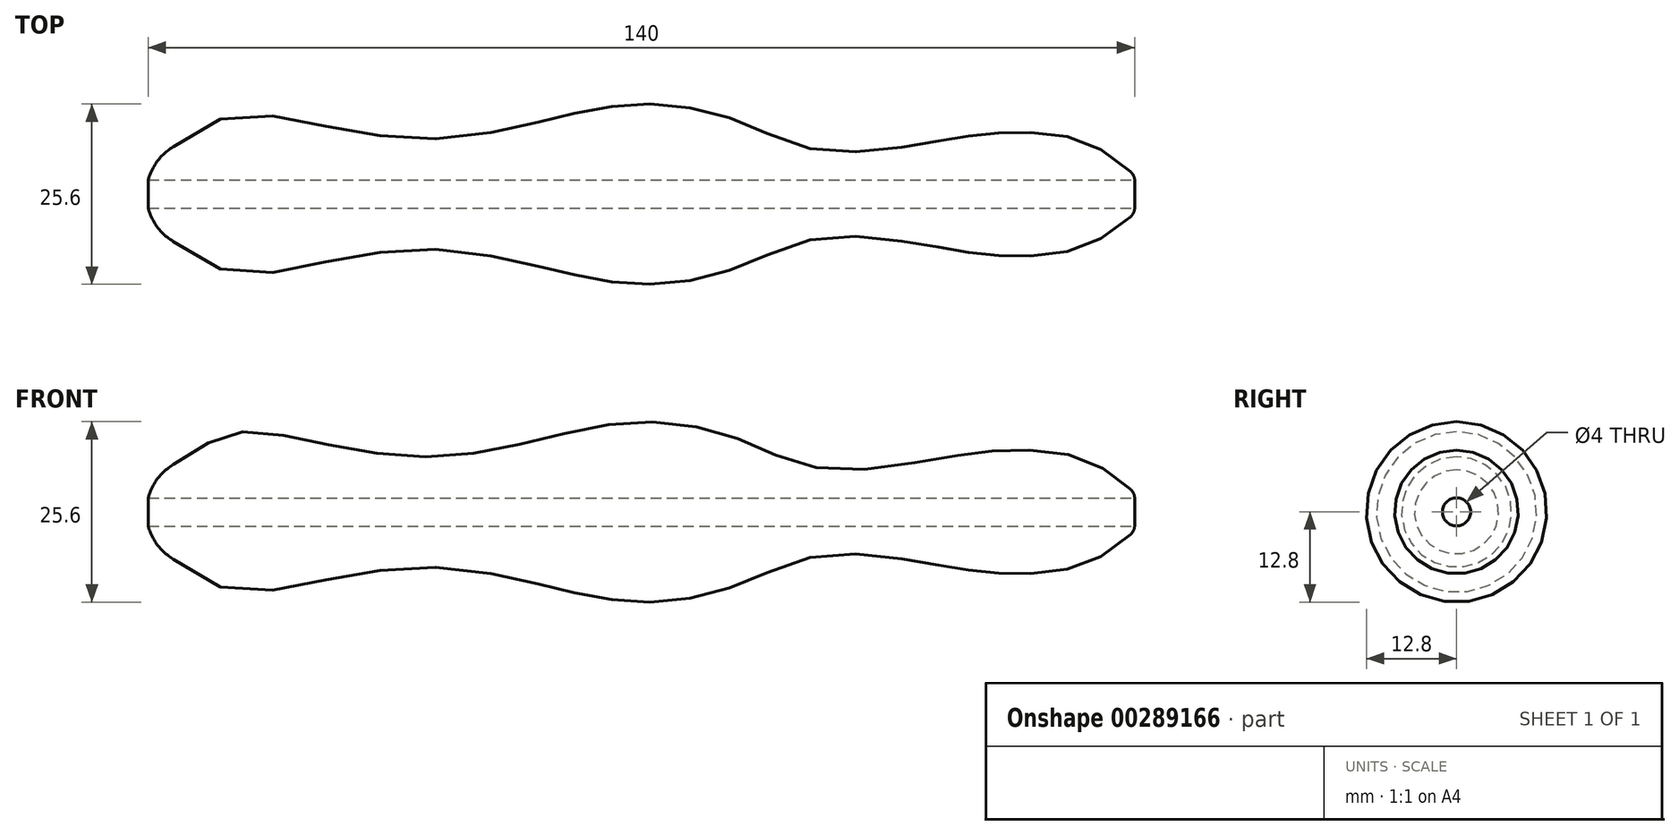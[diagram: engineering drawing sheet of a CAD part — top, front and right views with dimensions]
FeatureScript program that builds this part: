
annotation { "Feature Type Name" : "Feature", "Feature Type Description" : "" }
export const myFeature = defineFeature(function(context is Context, id is Id, definition is map)
    precondition{}
    {
        {
            var Q0;
            Q0=qCreatedBy(makeId("Top.planeOp"),FACE);
            var sketch = newSketch(context, id + "F0", { "sketchPlane" : qUnion([Q0])});
            skLineSegment(sketch, "E0", {"start": v(0, 0) * mm, "end": v(140, 0) * mm});
            skLineSegment(sketch, "E1", {"start": v(140, 2.71) * mm, "end": v(140, 0) * mm});
            skLineSegment(sketch, "E2", {"start": v(0, 0) * mm, "end": v(0, 5) * mm});
            skFitSpline(sketch, "E3", {"points": [v(0, 5) * mm, v(11.1, 10.96) * mm, v(23.25, 10.04) * mm, v(40.19, 7.83) * mm, v(56.02, 10.4) * mm, v(70.2, 12.8) * mm, v(83.64, 10.4) * mm, v(95.61, 6.17) * mm, v(112.74, 7.64) * mm, v(121.95, 8.75) * mm, v(132.81, 7.46) * mm, v(140, 2.71) * mm], "startDerivative": vector(166.86, 63.4) * mm, "endDerivative": vector(86.8, -71.08) * mm});
            skSolve(sketch);
        }
        {
            var Q0;
            Q0=makeQuery(id+"F0.imprint","IMPRINT",FACE,{"disambiguationData":[TD([[makeQuery(id+"F0.imprint","IMPRINT",EDGE,{"derivedFrom":sQuery(id+"F0.wireOp",EDGE,"E0")}),1.0]])]});
            var Q1;
            Q1=sQuery(id+"F0.wireOp",EDGE,"E0");
            revolve(context, id + "F1", {"entities" : qUnion([Q0]), "axis" : qUnion([Q1]), "revolveType" : RevolveType.FULL});
        }
        {
            var Q0;
            Q0=makeQuery(id+"F1.opRevolve","SWEPT_FACE",FACE,{"disambiguationData":[OSD([sQuery(id+"F0.wireOp",EDGE,"E1")])]});
            var sketch = newSketch(context, id + "F2", { "sketchPlane" : qUnion([Q0])});
            skCircle(sketch, "E4", {"center": v(0, 0) * mm, "radius": 2 * mm});
            skSolve(sketch);
        }
        {
            var Q0;
            Q0 = qSketchRegion(id + "F2", true);
            extrude(context, id + "F3", {"entities" : qUnion([Q0]), "operationType" : NewBodyOperationType.REMOVE, "endBound" : BoundingType.THROUGH_ALL, "oppositeDirection" : true, "depth" : 25.4 * mm});
        }
        {
            var Q0;
            Q0=makeQuery(id+"F1.opRevolve","SWEPT_EDGE",EDGE,{"disambiguationData":[OSD([sQuery(id+"F0.wireOp",EDGE,"E2"),sQuery(id+"F0.wireOp",EDGE,"E3")])]});
            fillet(context, id + "F4", {"entities" : qUnion([Q0]), "radius" : 7.62 * mm, "tangentPropagation" : true, "allowEdgeOverflow" : false});
        }
        {
            var Q0;
            Q0=makeQuery(id+"F1.opRevolve","SWEPT_EDGE",EDGE,{"disambiguationData":[OSD([sQuery(id+"F0.wireOp",EDGE,"E1"),sQuery(id+"F0.wireOp",EDGE,"E3")])]});
            fillet(context, id + "F5", {"entities" : qUnion([Q0]), "radius" : 1.78 * mm, "tangentPropagation" : true, "allowEdgeOverflow" : false});
        }
    });
